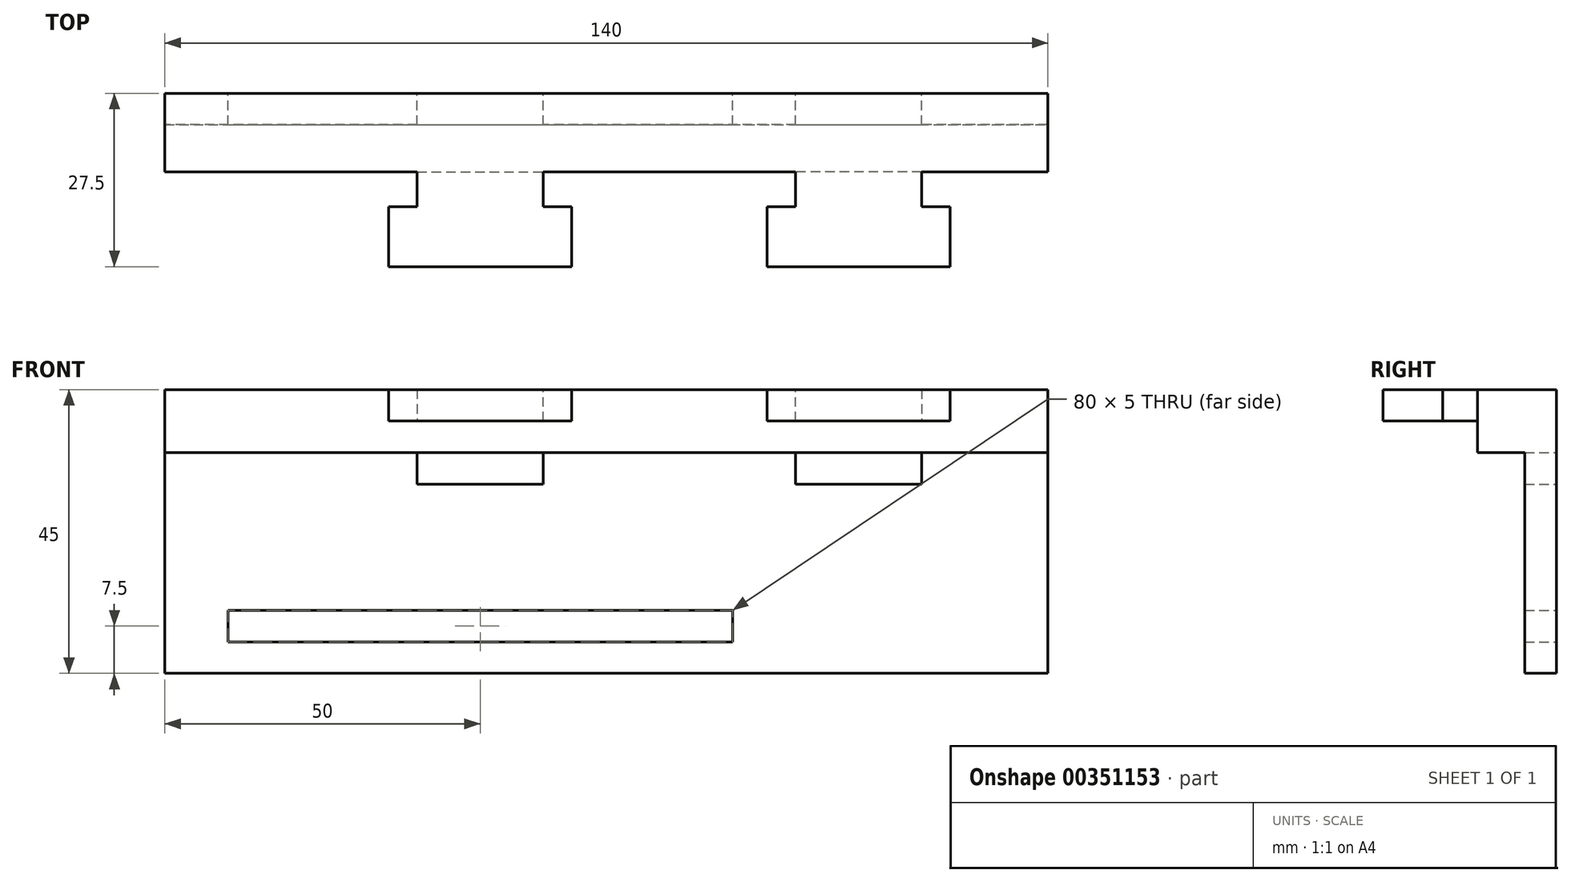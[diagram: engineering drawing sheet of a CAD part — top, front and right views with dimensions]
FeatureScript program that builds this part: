
annotation { "Feature Type Name" : "Feature", "Feature Type Description" : "" }
export const myFeature = defineFeature(function(context is Context, id is Id, definition is map)
    precondition{}
    {
        {
            var Q0;
            Q0=qCreatedBy(makeId("Front.planeOp"),FACE);
            var sketch = newSketch(context, id + "F0", { "sketchPlane" : qUnion([Q0])});
            skLineSegment(sketch, "E0.bottom", {"start": v(-75.34, 0) * mm, "end": v(64.66, 0) * mm});
            skLineSegment(sketch, "E0.top", {"start": v(-75.34, 45) * mm, "end": v(64.66, 45) * mm});
            skLineSegment(sketch, "E0.left", {"start": v(-75.34, 0) * mm, "end": v(-75.34, 45) * mm});
            skLineSegment(sketch, "E0.right", {"start": v(64.66, 0) * mm, "end": v(64.66, 45) * mm});
            skLineSegment(sketch, "E1", {"start": v(-75.34, 0) * mm, "end": v(-75.34, 5) * mm, "construction": true});
            skLineSegment(sketch, "E2", {"start": v(-75.34, 5) * mm, "end": v(-55.34, 5) * mm, "construction": true});
            skLineSegment(sketch, "E3.bottom", {"start": v(-55.34, 5) * mm, "end": v(14.66, 5) * mm});
            skLineSegment(sketch, "E3.top", {"start": v(-55.34, 10) * mm, "end": v(14.66, 10) * mm});
            skLineSegment(sketch, "E3.left", {"start": v(-55.34, 5) * mm, "end": v(-55.34, 10) * mm, "construction": true});
            skLineSegment(sketch, "E3.right", {"start": v(14.66, 5) * mm, "end": v(14.66, 10) * mm});
            skLineSegment(sketch, "E4", {"start": v(-55.34, 10) * mm, "end": v(-65.34, 10) * mm});
            skLineSegment(sketch, "E5", {"start": v(-65.34, 10) * mm, "end": v(-65.34, 5) * mm});
            skLineSegment(sketch, "E6", {"start": v(-65.34, 5) * mm, "end": v(-55.34, 5) * mm});
            skLineSegment(sketch, "E7", {"start": v(64.66, 45) * mm, "end": v(44.66, 45) * mm, "construction": true});
            skLineSegment(sketch, "E8", {"start": v(44.66, 45) * mm, "end": v(44.66, 40) * mm});
            skLineSegment(sketch, "E9", {"start": v(44.66, 40) * mm, "end": v(24.66, 40) * mm});
            skLineSegment(sketch, "E10", {"start": v(24.66, 40) * mm, "end": v(24.66, 45) * mm});
            skLineSegment(sketch, "E11", {"start": v(24.66, 45) * mm, "end": v(44.66, 45) * mm});
            skLineSegment(sketch, "E12", {"start": v(24.66, 40) * mm, "end": v(24.66, 35) * mm, "construction": true});
            skLineSegment(sketch, "E13", {"start": v(24.66, 35) * mm, "end": v(24.66, 30) * mm});
            skLineSegment(sketch, "E14", {"start": v(24.66, 30) * mm, "end": v(44.66, 30) * mm});
            skLineSegment(sketch, "E15", {"start": v(44.66, 30) * mm, "end": v(44.66, 35) * mm});
            skLineSegment(sketch, "E16", {"start": v(44.66, 35) * mm, "end": v(24.66, 35) * mm});
            skLineSegment(sketch, "E17", {"start": v(24.66, 40) * mm, "end": v(-15.34, 40) * mm, "construction": true});
            skLineSegment(sketch, "E18", {"start": v(-15.34, 40) * mm, "end": v(-15.34, 45) * mm});
            skLineSegment(sketch, "E19", {"start": v(-15.34, 45) * mm, "end": v(-35.34, 45) * mm});
            skLineSegment(sketch, "E20", {"start": v(-35.34, 45) * mm, "end": v(-35.34, 40) * mm});
            skLineSegment(sketch, "E21", {"start": v(-35.34, 40) * mm, "end": v(-15.34, 40) * mm});
            skLineSegment(sketch, "E22", {"start": v(-15.34, 40) * mm, "end": v(-15.34, 35) * mm, "construction": true});
            skLineSegment(sketch, "E23", {"start": v(-15.34, 35) * mm, "end": v(-35.34, 35) * mm});
            skLineSegment(sketch, "E24", {"start": v(-35.34, 35) * mm, "end": v(-35.34, 30) * mm});
            skLineSegment(sketch, "E25", {"start": v(-35.34, 30) * mm, "end": v(-15.34, 30) * mm});
            skLineSegment(sketch, "E26", {"start": v(-15.34, 30) * mm, "end": v(-15.34, 35) * mm});
            skSolve(sketch);
        }
        {
            var Q0;
            Q0=makeQuery(id+"F0.imprint","IMPRINT",FACE,{"disambiguationData":[TD([[makeQuery(id+"F0.imprint","IMPRINT",EDGE,{"derivedFrom":sQuery(id+"F0.wireOp",EDGE,"E0.bottom")}),1.0]])]});
            extrude(context, id + "F1", {"entities" : qUnion([Q0]), "depth" : 5 * mm});
        }
        {
            var Q0;
            Q0=makeQuery(id+"F1.opExtrude","CAP_FACE",FACE,{"disambiguationData":[OSD([sQuery(id+"F0.wireOp",EDGE,"E0.bottom"),sQuery(id+"F0.wireOp",EDGE,"E0.top"),sQuery(id+"F0.wireOp",EDGE,"E0.left"),sQuery(id+"F0.wireOp",EDGE,"E0.right"),sQuery(id+"F0.wireOp",EDGE,"E3.bottom"),sQuery(id+"F0.wireOp",EDGE,"E3.top"),sQuery(id+"F0.wireOp",EDGE,"E3.right"),sQuery(id+"F0.wireOp",EDGE,"E4"),sQuery(id+"F0.wireOp",EDGE,"E5"),sQuery(id+"F0.wireOp",EDGE,"E6"),sQuery(id+"F0.wireOp",EDGE,"E8"),sQuery(id+"F0.wireOp",EDGE,"E9"),sQuery(id+"F0.wireOp",EDGE,"E10"),sQuery(id+"F0.wireOp",EDGE,"E13"),sQuery(id+"F0.wireOp",EDGE,"E14"),sQuery(id+"F0.wireOp",EDGE,"E15"),sQuery(id+"F0.wireOp",EDGE,"E16"),sQuery(id+"F0.wireOp",EDGE,"E18"),sQuery(id+"F0.wireOp",EDGE,"E20"),sQuery(id+"F0.wireOp",EDGE,"E21"),sQuery(id+"F0.wireOp",EDGE,"E23"),sQuery(id+"F0.wireOp",EDGE,"E24"),sQuery(id+"F0.wireOp",EDGE,"E25"),sQuery(id+"F0.wireOp",EDGE,"E26")])],"isStart":false});
            var sketch = newSketch(context, id + "F2", { "sketchPlane" : qUnion([Q0])});
            skLineSegment(sketch, "E27", {"start": v(-75.34, 45) * mm, "end": v(-75.34, 35) * mm});
            skLineSegment(sketch, "E28", {"start": v(-75.34, 35) * mm, "end": v(64.66, 35) * mm});
            skLineSegment(sketch, "E29", {"start": v(64.66, 35) * mm, "end": v(64.66, 45) * mm});
            skLineSegment(sketch, "E30", {"start": v(64.66, 45) * mm, "end": v(-75.34, 45) * mm});
            skSolve(sketch);
        }
        {
            var Q0;
            Q0=makeQuery(id+"F0.imprint","IMPRINT",FACE,{"disambiguationData":[TD([[makeQuery(id+"F0.imprint","IMPRINT",EDGE,{"derivedFrom":sQuery(id+"F0.wireOp",EDGE,"E18")}),1.0]])]});
            var Q1;
            Q1=makeQuery(id+"F0.imprint","IMPRINT",FACE,{"disambiguationData":[TD([[makeQuery(id+"F0.imprint","IMPRINT",EDGE,{"derivedFrom":sQuery(id+"F0.wireOp",EDGE,"E8")}),-1.0]])]});
            extrude(context, id + "F3", {"entities" : qUnion([Q0, Q1]), "operationType" : NewBodyOperationType.ADD, "depth" : 27.5 * mm});
        }
        {
            var Q0;
            {var subQ3=sQuery(id+"F2.wireOp",EDGE,"E27");Q0=makeQuery(id+"F2.imprint","IMPRINT",FACE,{"disambiguationData":[TD([[makeQuery(id+"F2.imprint","IMPRINT",EDGE,{"derivedFrom":subQ3}),-1.0]])]});}
            extrude(context, id + "F4", {"entities" : qUnion([Q0]), "operationType" : NewBodyOperationType.ADD, "depth" : 7.5 * mm});
        }
        {
            var Q0;
            Q0=makeQuery(id+"F3.opExtrude","CAP_FACE",FACE,{"disambiguationData":[OSD([sQuery(id+"F0.wireOp",EDGE,"E18"),sQuery(id+"F0.wireOp",EDGE,"E19"),sQuery(id+"F0.wireOp",EDGE,"E20"),sQuery(id+"F0.wireOp",EDGE,"E21")])],"isStart":false});
            var sketch = newSketch(context, id + "F5", { "sketchPlane" : qUnion([Q0])});
            skLineSegment(sketch, "E31.bottom", {"start": v(-15.34, 45) * mm, "end": v(-10.84, 45) * mm});
            skLineSegment(sketch, "E31.top", {"start": v(-15.34, 40) * mm, "end": v(-10.84, 40) * mm});
            skLineSegment(sketch, "E31.left", {"start": v(-15.34, 45) * mm, "end": v(-15.34, 40) * mm});
            skLineSegment(sketch, "E31.right", {"start": v(-10.84, 45) * mm, "end": v(-10.84, 40) * mm});
            skLineSegment(sketch, "E32.bottom", {"start": v(-35.34, 45) * mm, "end": v(-39.84, 45) * mm});
            skLineSegment(sketch, "E32.top", {"start": v(-35.34, 40) * mm, "end": v(-39.84, 40) * mm});
            skLineSegment(sketch, "E32.left", {"start": v(-35.34, 45) * mm, "end": v(-35.34, 40) * mm});
            skLineSegment(sketch, "E32.right", {"start": v(-39.84, 45) * mm, "end": v(-39.84, 40) * mm});
            skSolve(sketch);
        }
        {
            var Q0;
            Q0=makeQuery(id+"F5.imprint","IMPRINT",FACE,{"disambiguationData":[TD([[makeQuery(id+"F5.imprint","IMPRINT",EDGE,{"derivedFrom":sQuery(id+"F5.wireOp",EDGE,"E32.bottom")}),1.0]])]});
            var Q1;
            Q1=makeQuery(id+"F5.imprint","IMPRINT",FACE,{"disambiguationData":[TD([[makeQuery(id+"F5.imprint","IMPRINT",EDGE,{"derivedFrom":sQuery(id+"F5.wireOp",EDGE,"E31.bottom")}),-1.0]])]});
            extrude(context, id + "F6", {"entities" : qUnion([Q0, Q1]), "operationType" : NewBodyOperationType.ADD, "depth" : -9.5 * mm});
        }
        {
            var Q0;
            Q0=makeQuery(id+"F3.opExtrude","CAP_FACE",FACE,{"disambiguationData":[OSD([sQuery(id+"F0.wireOp",EDGE,"E8"),sQuery(id+"F0.wireOp",EDGE,"E9"),sQuery(id+"F0.wireOp",EDGE,"E10"),sQuery(id+"F0.wireOp",EDGE,"E11")])],"isStart":false});
            var sketch = newSketch(context, id + "F7", { "sketchPlane" : qUnion([Q0])});
            skLineSegment(sketch, "E33.bottom", {"start": v(44.66, 45) * mm, "end": v(49.16, 45) * mm});
            skLineSegment(sketch, "E33.top", {"start": v(44.66, 40) * mm, "end": v(49.16, 40) * mm});
            skLineSegment(sketch, "E33.left", {"start": v(44.66, 45) * mm, "end": v(44.66, 40) * mm});
            skLineSegment(sketch, "E33.right", {"start": v(49.16, 45) * mm, "end": v(49.16, 40) * mm});
            skLineSegment(sketch, "E34.bottom", {"start": v(24.66, 45) * mm, "end": v(20.16, 45) * mm});
            skLineSegment(sketch, "E34.top", {"start": v(24.66, 40) * mm, "end": v(20.16, 40) * mm});
            skLineSegment(sketch, "E34.left", {"start": v(24.66, 45) * mm, "end": v(24.66, 40) * mm});
            skLineSegment(sketch, "E34.right", {"start": v(20.16, 45) * mm, "end": v(20.16, 40) * mm});
            skSolve(sketch);
        }
        {
            var Q0;
            Q0=makeQuery(id+"F7.imprint","IMPRINT",FACE,{"disambiguationData":[TD([[makeQuery(id+"F7.imprint","IMPRINT",EDGE,{"derivedFrom":sQuery(id+"F7.wireOp",EDGE,"E34.bottom")}),1.0]])]});
            var Q1;
            Q1=makeQuery(id+"F7.imprint","IMPRINT",FACE,{"disambiguationData":[TD([[makeQuery(id+"F7.imprint","IMPRINT",EDGE,{"derivedFrom":sQuery(id+"F7.wireOp",EDGE,"E33.bottom")}),-1.0]])]});
            extrude(context, id + "F8", {"entities" : qUnion([Q0, Q1]), "operationType" : NewBodyOperationType.ADD, "depth" : -9.5 * mm});
        }
    });
